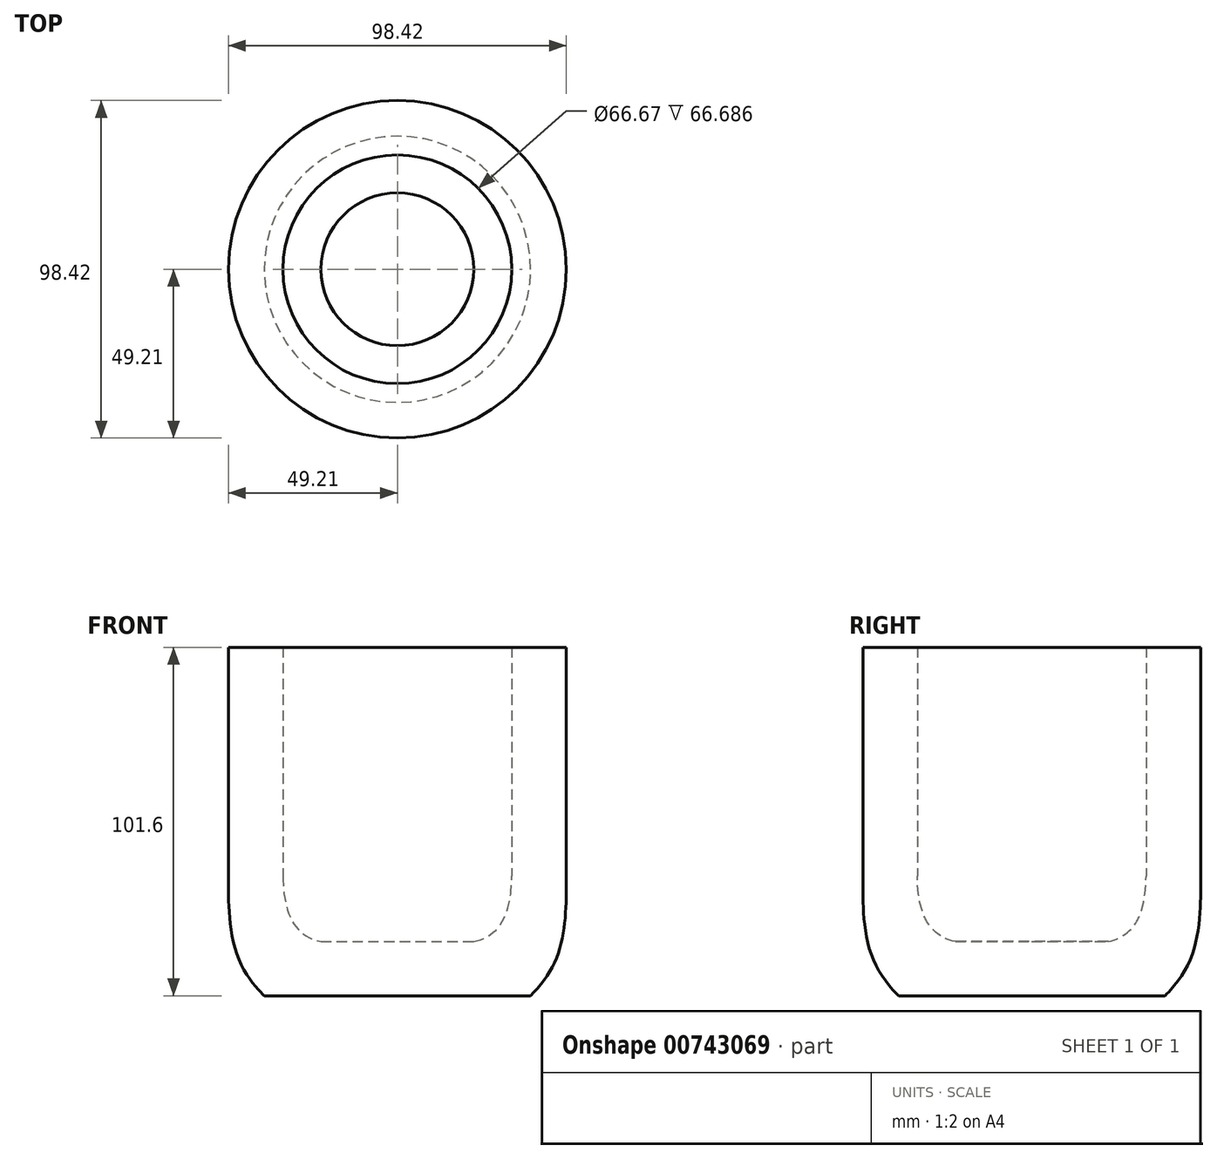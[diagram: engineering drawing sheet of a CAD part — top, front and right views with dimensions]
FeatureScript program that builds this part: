
annotation { "Feature Type Name" : "Feature", "Feature Type Description" : "" }
export const myFeature = defineFeature(function(context is Context, id is Id, definition is map)
    precondition{}
    {
        {
            var Q0;
            Q0=qCreatedBy(makeId("Front.planeOp"),FACE);
            var sketch = newSketch(context, id + "F0", { "sketchPlane" : qUnion([Q0])});
            skLineSegment(sketch, "E0.bottom", {"start": v(0, 0) * mm, "end": v(38.8, 0) * mm});
            skLineSegment(sketch, "E0.top", {"start": v(33.34, 101.6) * mm, "end": v(49.21, 101.6) * mm});
            skLineSegment(sketch, "E0.left", {"start": v(0, 0) * mm, "end": v(0, 101.6) * mm, "construction": true});
            skLineSegment(sketch, "E0.right", {"start": v(49.21, 31.66) * mm, "end": v(49.21, 101.6) * mm});
            skLineSegment(sketch, "E1.MirrorCS", {"start": v(-33.34, 101.6) * mm, "end": v(-49.21, 101.6) * mm});
            skLineSegment(sketch, "E2.MirrorCS", {"start": v(-49.21, 31.66) * mm, "end": v(-49.21, 101.6) * mm});
            skLineSegment(sketch, "E3.MirrorCS", {"start": v(0, 0) * mm, "end": v(-38.8, 0) * mm});
            skFitSpline(sketch, "E4", {"points": [v(49.21, 31.66) * mm, v(46.36, 10.93) * mm, v(38.8, 0) * mm], "startDerivative": vector(0, -26.22) * mm, "endDerivative": vector(-9.37, -8.93) * mm});
            skLineSegment(sketch, "E5.bottom", {"start": v(22.28, 15.88) * mm, "end": v(-22.28, 15.88) * mm});
            skLineSegment(sketch, "E5.left", {"start": v(33.34, 34.91) * mm, "end": v(33.34, 101.6) * mm});
            skLineSegment(sketch, "E5.right", {"start": v(-33.34, 34.91) * mm, "end": v(-33.34, 101.6) * mm});
            skPoint(sketch, "E5.middle", {"position": v(0, 70.05) * mm});
            skFitSpline(sketch, "E6", {"points": [v(33.34, 34.91) * mm, v(29.26, 19.78) * mm, v(22.28, 15.88) * mm], "startDerivative": vector(0, -29.2) * mm, "endDerivative": vector(-11.97, -0.92) * mm});
            skPoint(sketch, "E7.orphan", {"position": v(-33.34, 124.22) * mm});
            skPoint(sketch, "E8.orphan", {"position": v(33.34, 124.22) * mm});
            skPoint(sketch, "E9.orphan", {"position": v(0, 101.6) * mm});
            skPoint(sketch, "E10.orphan", {"position": v(33.34, 15.88) * mm});
            skPoint(sketch, "E11.orphan", {"position": v(49.21, 0) * mm});
            skFitSpline(sketch, "E12.MirrorCS", {"points": [v(-33.34, 34.91) * mm, v(-29.26, 19.78) * mm, v(-22.28, 15.88) * mm], "startDerivative": vector(0, -29.2) * mm, "endDerivative": vector(11.97, -0.92) * mm});
            skFitSpline(sketch, "E13.MirrorCS", {"points": [v(-49.21, 31.66) * mm, v(-46.36, 10.93) * mm, v(-38.8, 0) * mm], "startDerivative": vector(0, -26.22) * mm, "endDerivative": vector(9.37, -8.93) * mm});
            skPoint(sketch, "E14.orphan", {"position": v(-49.21, 0) * mm});
            skPoint(sketch, "E15.orphan", {"position": v(-33.34, 15.88) * mm});
            skLineSegment(sketch, "E16", {"start": v(0, 0) * mm, "end": v(0, 15.88) * mm});
            skSolve(sketch);
        }
        {
            var Q0;
            Q0=makeQuery(id+"F0.imprint","IMPRINT",FACE,{"disambiguationData":[TD([[makeQuery(id+"F0.imprint","IMPRINT",EDGE,{"derivedFrom":sQuery(id+"F0.wireOp",EDGE,"E0.bottom")}),1.0]])]});
            var Q1;
            Q1=sQuery(id+"F0.wireOp",EDGE,"E16");
            revolve(context, id + "F1", {"surfaceOperationType" : NewSurfaceOperationType.NEW, "entities" : qUnion([Q0]), "axis" : qUnion([Q1]), "revolveType" : RevolveType.FULL});
        }
    });
